# Revit family: Sink-Wall-Caroma Cleaners1
name_source: partatom
category: Plumbing Fixtures
revit_build: Autodesk Revit Architecture 2012 (Build: 20110916_2132(x64)
units: mm (PartAtom-declared; Revit-internal decimal feet)

## types (1)
- Cleaners Sink
    Assembly Code = D2010440
    BowlCapacity_ANZRS = 0.03 m³
    CW Connection = No
    Cost = 889 $
    Default Elevation = 560 mm  [stored 1.83727 ft]
    Depth_ANZRS = 285 mm  [stored 0.935039 ft]
    Description = Caroma Cleaners Sink
    Grate = Yes
    Guard = Rubber-Black-Caroma
    HW Connection = No
    Keynote = CS
    Length_ANZRS = 575 mm
    Manufacturer = Caroma
    Material_ANZRS = Porcelain-White-Caroma
    Model = 811592W
    PlumbingMaterial_ANZRS = PVC-White-Caroma
    Type Comments = Includes buffer, Centre back outlet, 27L capacity
    URL = http://www.caroma.com.au
    Vent Connection = No
    WFU = 2
    Waste = Metal-Chrome-Caroma
    Waste Connection = Yes
    Width_ANZRS = 435 mm  [stored 1.42717 ft]

note: [stored X ft] marks values corroborated as IEEE doubles in the binary element streams (Revit-internal decimal feet)

## geometry (parser evidence)
native form markers: Blend x6, Sweep x2
no freeform markers — native parametric forms only
